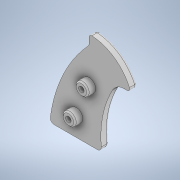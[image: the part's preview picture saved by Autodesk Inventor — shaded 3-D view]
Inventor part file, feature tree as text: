
AUTODESK INVENTOR PART (.ipt)
format: ipt  version: 2021 (Build 250183000, 183)  size: 174,080 bytes
history: native  units: in
note: dims shown in document units (in); Inventor stores cm internally (conversion verified against a paired STEP export)
features: chamfer x3, extrude x2, sketch x2, fillet x1
ambient origin geometry x8: Origin, YZ Plane, XZ Plane, XY Plane, X Axis, Y Axis, Z Axis, Center Point
bodies: Solid1 (feature_tree)
feature tree (8):
  extrude  "Extrusion1"  Depth=0.0787in
  fillet  "Fillet1"  Radius=0.2362in
  extrude  "Extrusion2"  Depth=0.0787in TaperAngle=45.0deg
  chamfer  "Chamfer1"  Distance=0.0787in Angle=45.0deg
  chamfer  "Chamfer2"  [1 undecoded]
  chamfer  "Chamfer3"  [1 undecoded]
  sketch  "Sketch1"  dims[d0=0.2362in d1=0.0in d2=0.0787in d3=0.2362in d4=0.0in]
  sketch  "Sketch2"  dims[d5=0.0394in d6=0.0787in d7=45.0deg d8=0.0787in d9=0.0787in d10=45.0deg d11=0.0787in d12=0.0787in d13=45.0deg]
note: 2 required parameter values undecoded (feature->parameter linkage not recoverable at this tier; creation-order binding heuristic only, values carry confidence <= 0.55)
